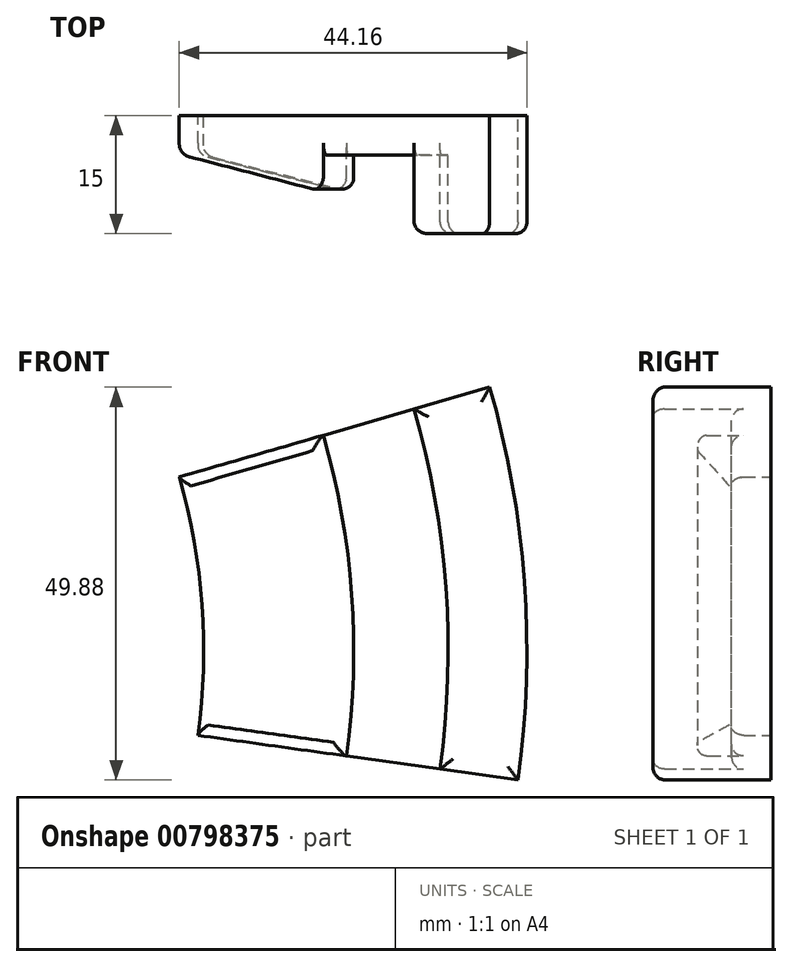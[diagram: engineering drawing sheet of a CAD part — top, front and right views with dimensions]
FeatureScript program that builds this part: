
annotation { "Feature Type Name" : "Feature", "Feature Type Description" : "" }
export const myFeature = defineFeature(function(context is Context, id is Id, definition is map)
    precondition{}
    {
        {
            var Q0;
            Q0=qCreatedBy(makeId("Front.planeOp"),FACE);
            var sketch = newSketch(context, id + "F0", { "sketchPlane" : qUnion([Q0])});
            skCircle(sketch, "E0", {"center": v(0, 0) * mm, "radius": 120 * mm});
            skCircle(sketch, "E1", {"center": v(0, 0) * mm, "radius": 110 * mm});
            skCircle(sketch, "E2", {"center": v(0, 0) * mm, "radius": 98 * mm});
            skCircle(sketch, "E3", {"center": v(0, 0) * mm, "radius": 78.95 * mm});
            skLineSegment(sketch, "E4", {"start": v(0, 0) * mm, "end": v(115.27, 33.35) * mm});
            skLineSegment(sketch, "E5", {"start": v(0, 0) * mm, "end": v(118.86, -16.53) * mm});
            skSolve(sketch);
        }
        {
            var Q0;
            {var subQ0=sQuery(id+"F0.wireOp",EDGE,"E4");var subQ1=sQuery(id+"F0.wireOp",EDGE,"E2");var subQ2=makeQuery(id+"F0.imprint","INTERSECT",VERTEX,{"derivedFrom":[subQ1,subQ0]});Q0=makeQuery(id+"F0.imprint","IMPRINT",FACE,{"disambiguationData":[TD([[makeQuery(id+"F0.imprint","IMPRINT",EDGE,{"disambiguationData":[TD([[subQ2,1.0]])],"derivedFrom":subQ1}),1.0]])]});}
            extrude(context, id + "F1", {"entities" : qUnion([Q0]), "depth" : 10 * mm, "offsetDistance" : 25 * mm});
        }
        {
            var Q0;
            {var subQ0=sQuery(id+"F0.wireOp",EDGE,"E4");var subQ1=sQuery(id+"F0.wireOp",EDGE,"E1");var subQ2=makeQuery(id+"F0.imprint","INTERSECT",VERTEX,{"derivedFrom":[subQ1,subQ0]});Q0=makeQuery(id+"F0.imprint","IMPRINT",FACE,{"disambiguationData":[TD([[makeQuery(id+"F0.imprint","IMPRINT",EDGE,{"disambiguationData":[TD([[subQ2,1.0]])],"derivedFrom":subQ1}),1.0]])]});}
            extrude(context, id + "F2", {"entities" : qUnion([Q0]), "operationType" : NewBodyOperationType.ADD, "depth" : 5 * mm, "offsetDistance" : 25 * mm});
        }
        {
            var Q0;
            {var subQ0=sQuery(id+"F0.wireOp",EDGE,"E4");var subQ1=sQuery(id+"F0.wireOp",EDGE,"E0");var subQ2=makeQuery(id+"F0.imprint","INTERSECT",VERTEX,{"derivedFrom":[subQ1,subQ0]});Q0=makeQuery(id+"F0.imprint","IMPRINT",FACE,{"disambiguationData":[TD([[makeQuery(id+"F0.imprint","IMPRINT",EDGE,{"disambiguationData":[TD([[subQ2,1.0]])],"derivedFrom":subQ1}),1.0]])]});}
            extrude(context, id + "F3", {"entities" : qUnion([Q0]), "operationType" : NewBodyOperationType.ADD, "depth" : 15 * mm, "offsetDistance" : 25 * mm});
        }
        {
            var Q0;
            Q0=makeQuery(id+"F1.opExtrude","CAP_EDGE",EDGE,{"disambiguationData":[OSD([sQuery(id+"F0.wireOp",EDGE,"E3")])],"isStart":false});
            chamfer(context, id + "F4", {"entities" : qUnion([Q0]), "chamferType" : ChamferType.TWO_OFFSETS, "width1" : 5 * mm, "oppositeDirection" : false, "width2" : 20 * mm, "tangentPropagation" : true});
        }
        {
            var Q0;
            Q0=makeQuery(id+"F2.opExtrude","CAP_EDGE",EDGE,{"disambiguationData":[OSD([sQuery(id+"F0.wireOp",EDGE,"E1")])],"isStart":false});
            var Q1;
            Q1=makeQuery(id+"F2.opExtrude","CAP_EDGE",EDGE,{"disambiguationData":[OSD([sQuery(id+"F0.wireOp",EDGE,"E2")])],"isStart":false});
            var Q2;
            Q2=makeQuery(id+"F4.opChamfer","BLEND_EDGE",EDGE,{"blendedFrom":[makeQuery(id+"F1.opExtrude","CAP_EDGE",EDGE,{"disambiguationData":[OSD([sQuery(id+"F0.wireOp",EDGE,"E3")])],"isStart":false}),makeQuery(id+"F1.opExtrude","SWEPT_FACE",FACE,{"disambiguationData":[OSD([sQuery(id+"F0.wireOp",EDGE,"E2")])]})],"blendedInto":[makeQuery(id+"F1.opExtrude","SWEPT_FACE",FACE,{"disambiguationData":[OSD([sQuery(id+"F0.wireOp",EDGE,"E2")])]})]});
            var Q3;
            Q3=makeQuery(id+"F3.opExtrude","CAP_EDGE",EDGE,{"disambiguationData":[OSD([sQuery(id+"F0.wireOp",EDGE,"E1")])],"isStart":false});
            var Q4;
            Q4=makeQuery(id+"F3.opExtrude","CAP_EDGE",EDGE,{"disambiguationData":[OSD([sQuery(id+"F0.wireOp",EDGE,"E0")])],"isStart":false});
            var Q5;
            {var subQ0=sQuery(id+"F0.wireOp",EDGE,"E5");Q5=makeQuery(id+"F4.opChamfer","BLEND_EDGE",EDGE,{"blendedFrom":[makeQuery(id+"F1.opExtrude","CAP_EDGE",EDGE,{"disambiguationData":[OSD([sQuery(id+"F0.wireOp",EDGE,"E3")])],"isStart":false}),makeQuery(id+"F3.boolean.opBoolean","MERGE",FACE,{"derivedFrom":[makeQuery(id+"F2.boolean.opBoolean","MERGE",FACE,{"derivedFrom":[makeQuery(id+"F1.opExtrude","SWEPT_FACE",FACE,{"disambiguationData":[OSD([subQ0])]}),makeQuery(id+"F2.opExtrude","SWEPT_FACE",FACE,{"disambiguationData":[OSD([subQ0])]})]}),makeQuery(id+"F3.opExtrude","SWEPT_FACE",FACE,{"disambiguationData":[OSD([subQ0])]})]})],"blendedInto":[makeQuery(id+"F3.boolean.opBoolean","MERGE",FACE,{"derivedFrom":[makeQuery(id+"F2.boolean.opBoolean","MERGE",FACE,{"derivedFrom":[makeQuery(id+"F1.opExtrude","SWEPT_FACE",FACE,{"disambiguationData":[OSD([subQ0])]}),makeQuery(id+"F2.opExtrude","SWEPT_FACE",FACE,{"disambiguationData":[OSD([subQ0])]})]}),makeQuery(id+"F3.opExtrude","SWEPT_FACE",FACE,{"disambiguationData":[OSD([subQ0])]})]})]});}
            var Q6;
            Q6=makeQuery(id+"F3.opExtrude","CAP_EDGE",EDGE,{"disambiguationData":[OSD([sQuery(id+"F0.wireOp",EDGE,"E5")])],"isStart":false});
            var Q7;
            Q7=makeQuery(id+"F3.opExtrude","CAP_EDGE",EDGE,{"disambiguationData":[OSD([sQuery(id+"F0.wireOp",EDGE,"E4")])],"isStart":false});
            var Q8;
            {var subQ0=sQuery(id+"F0.wireOp",EDGE,"E4");Q8=makeQuery(id+"F4.opChamfer","BLEND_EDGE",EDGE,{"blendedFrom":[makeQuery(id+"F1.opExtrude","CAP_EDGE",EDGE,{"disambiguationData":[OSD([sQuery(id+"F0.wireOp",EDGE,"E3")])],"isStart":false}),makeQuery(id+"F3.boolean.opBoolean","MERGE",FACE,{"derivedFrom":[makeQuery(id+"F2.boolean.opBoolean","MERGE",FACE,{"derivedFrom":[makeQuery(id+"F1.opExtrude","SWEPT_FACE",FACE,{"disambiguationData":[OSD([subQ0])]}),makeQuery(id+"F2.opExtrude","SWEPT_FACE",FACE,{"disambiguationData":[OSD([subQ0])]})]}),makeQuery(id+"F3.opExtrude","SWEPT_FACE",FACE,{"disambiguationData":[OSD([subQ0])]})]})],"blendedInto":[makeQuery(id+"F3.boolean.opBoolean","MERGE",FACE,{"derivedFrom":[makeQuery(id+"F2.boolean.opBoolean","MERGE",FACE,{"derivedFrom":[makeQuery(id+"F1.opExtrude","SWEPT_FACE",FACE,{"disambiguationData":[OSD([subQ0])]}),makeQuery(id+"F2.opExtrude","SWEPT_FACE",FACE,{"disambiguationData":[OSD([subQ0])]})]}),makeQuery(id+"F3.opExtrude","SWEPT_FACE",FACE,{"disambiguationData":[OSD([subQ0])]})]})]});}
            var Q9;
            Q9=makeQuery(id+"F2.opExtrude","CAP_EDGE",EDGE,{"disambiguationData":[OSD([sQuery(id+"F0.wireOp",EDGE,"E4")])],"isStart":false});
            var Q10;
            Q10=makeQuery(id+"F2.opExtrude","CAP_EDGE",EDGE,{"disambiguationData":[OSD([sQuery(id+"F0.wireOp",EDGE,"E5")])],"isStart":false});
            var Q11;
            {var subQ0=sQuery(id+"F0.wireOp",EDGE,"E3");Q11=makeQuery(id+"F4.opChamfer","BLEND_EDGE",EDGE,{"blendedFrom":[makeQuery(id+"F1.opExtrude","CAP_EDGE",EDGE,{"disambiguationData":[OSD([subQ0])],"isStart":false}),makeQuery(id+"F1.opExtrude","SWEPT_FACE",FACE,{"disambiguationData":[OSD([subQ0])]})],"blendedInto":[makeQuery(id+"F1.opExtrude","SWEPT_FACE",FACE,{"disambiguationData":[OSD([subQ0])]})]});}
            fillet(context, id + "F5", {"entities" : qUnion([Q0, Q1, Q2, Q3, Q4, Q5, Q6, Q7, Q8, Q9, Q10, Q11]), "radius" : 1.5 * mm, "tangentPropagation" : true, "allowEdgeOverflow" : false});
        }
    });
